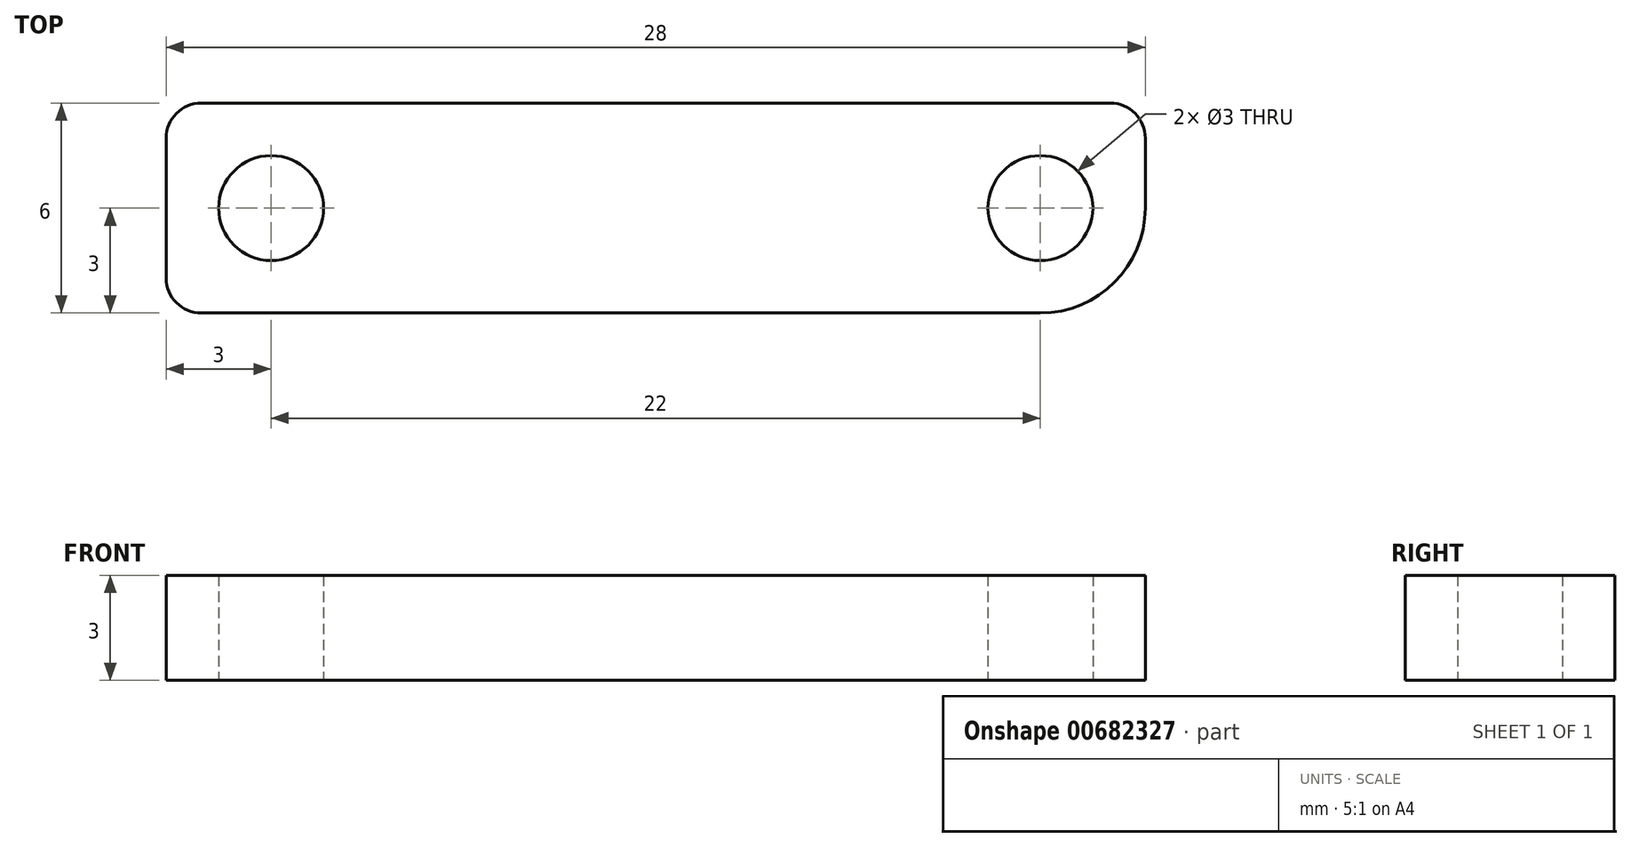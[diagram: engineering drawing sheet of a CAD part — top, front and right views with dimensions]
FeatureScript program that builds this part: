
annotation { "Feature Type Name" : "Feature", "Feature Type Description" : "" }
export const myFeature = defineFeature(function(context is Context, id is Id, definition is map)
    precondition{}
    {
        {
            var Q0;
            Q0=qCreatedBy(makeId("Top.planeOp"),FACE);
            var sketch = newSketch(context, id + "F0", { "sketchPlane" : qUnion([Q0])});
            skLineSegment(sketch, "E0.bottom", {"start": v(1, 0) * mm, "end": v(25, 0) * mm});
            skLineSegment(sketch, "E0.top", {"start": v(1, 6) * mm, "end": v(27, 6) * mm});
            skLineSegment(sketch, "E0.left", {"start": v(0, 1) * mm, "end": v(0, 5) * mm});
            skLineSegment(sketch, "E0.right", {"start": v(28, 3) * mm, "end": v(28, 5) * mm});
            skPoint(sketch, "E1.visualSharp", {"position": v(28, 6) * mm});
            skArc(sketch, "E1.filletArc", {"start": v(28, 5) * mm, "mid": v(27.7, 5.7) * mm, "end": v(27, 6) * mm});
            skPoint(sketch, "E2.visualSharp", {"position": v(0, 6) * mm});
            skArc(sketch, "E2.filletArc", {"start": v(1, 6) * mm, "mid": v(0.3, 5.7) * mm, "end": v(0, 5) * mm});
            skPoint(sketch, "E3.visualSharp", {"position": v(0, 0) * mm});
            skArc(sketch, "E3.filletArc", {"start": v(0, 1) * mm, "mid": v(0.3, 0.3) * mm, "end": v(1, 0) * mm});
            skPoint(sketch, "E4.visualSharp", {"position": v(28, 0) * mm});
            skArc(sketch, "E4.filletArc", {"start": v(25, 0) * mm, "mid": v(27.12, 0.88) * mm, "end": v(28, 3) * mm});
            skCircle(sketch, "E5", {"center": v(25, 3) * mm, "radius": 1.5 * mm});
            skLineSegment(sketch, "E6", {"start": v(-7, 3) * mm, "end": v(28, 3) * mm, "construction": true});
            skCircle(sketch, "E7", {"center": v(3, 3) * mm, "radius": 1.5 * mm});
            skSolve(sketch);
        }
        {
            var Q0;
            Q0 = qSketchRegion(id + "F0", true);
            extrude(context, id + "F1", {"entities" : qUnion([Q0]), "depth" : 3 * mm, "offsetDistance" : 25 * mm});
        }
    });
